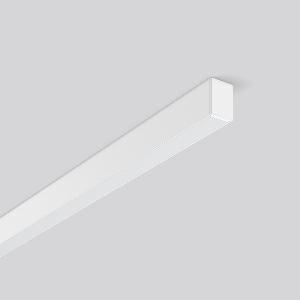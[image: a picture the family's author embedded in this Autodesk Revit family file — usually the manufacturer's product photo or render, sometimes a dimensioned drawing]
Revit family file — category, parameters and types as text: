
# Revit family: less_is_more_27_312200_002_1_4f38
name_source: partatom
category: Lighting Fixtures
units: mm (PartAtom-declared; Revit-internal decimal feet)

## family parameters
Cut with Voids When Loaded = No
Host = Face
Light Source = No
Part Type = Normal
Room Calculation Point = No
Round Connector Dimension = Use Diameter
Shared = No

## types (1)
- LESS IS MORE 27 (1 x LED Modul 840, 2900 lm, 4000)
    Apparent Load = 39 VA
    CIE Flux Codes = 48 79 96 100 100
    Color Rendering = 80
    Color Temperature = 4000
    Default Elevation = 1800 mm
    Description = Series: LESS IS MORE 27
Ceiling and wall luminaire with slim design. Housing: extruded aluminium profile, powder-coated. End cap aluminium powder-coated. Diffuser made of non-yellowing plastic (PMMA), opal. Suitable for Ceiling mounting, Wall (surface). External driver with connecting cable. 
Colour: traffic white, matt (RAL 9016)
Length: 1512 mm
Width: 28 mm
Height: 38 mm
Lamp: LED
Socket: without socket
Colour temperature: 4000K
Colour rendering index (CRI): 82
System power: 39 W
Rated luminous flux: 2900 lm
Luminous efficiency: 74 lm/W
Control gear: Regulated power supply
Protection class: II
Type of protection: IP 20
    Height = 38 mm
    Lamp = 1 x LED Modul 840
    Lamp Light Flux = 2900 lm
    Lamp count = 1
    Length = 1512 mm
    Lifetime = 50000 h
    Luminous efficacy = 74 lm/W
    Manufacturer = RZB
    ModVariant = No
    Model = 312200.002.1
    Mounting Place = Ceiling, Wall
    Mounting Type = Surface mounted
    Number of Poles = 1
    OnlyDefault = Yes
    Power Factor = 1
    Product Name = LESS IS MORE 27
    Product group = Surface mounted LED linear luminaires
    ProductGroupID = 307
    Protection Class = Protection class II
    Protection Degree = IP 20
    RLX_Detail_Level = 1
    RLX_Emergency_Light_Flux = 0 lm
    RLX_Emergency_Type = 0
    RLX_Emergency_Type_DB = No
    RlxData = <blob elided: 22809 chars, md5=b264bac4>
    Socket = socket
    Standby Power = 0 W
    System Light Flux = 2900 lm
    System Power = 39 W
    Type Comments = Product without accessories
    Type Image = 312196.002.jpg
    URL = http://relux.com
    VarID = ---
    Voltage = 230 V
    Voltage Range = 220-240 V
    Weight = 0.00 kg
    Width = 28 mm

## geometry (parser evidence)
native form markers: Blend x4, Sweep x10
no freeform markers — native parametric forms only
